# Revit family: 310-WC-4.8
name_source: partatom
category: Plumbing Fixtures
revit_build: Autodesk Revit 2014 (Build: 20130308_1515(x64)
units: mm (PartAtom-declared; Revit-internal decimal feet)

## types (1)
- 310-WC-4.8
    CW Connection = Yes
    Certification = http://www.helvex.com.mx
    Chrome = Brass Chromed
    Compliance = NOM-005-CONAGUA-1996
    Connection = 1" Feeding Connection
    Description = 1.268 gpf 32 Or 38 Exposed WC Flush Valve With Treadle
    Documentation = http://www.helvex.com.mx
    Features = To Be Used With 3/4" (19 mm) Spud
    Manufacturer = Helvex
    Max. Working Pressure = 85.3 psi
    Maximum Consumption = 1.26 gpf
    Min. Working Pressure = 14.2 psi
    Model = 310-WC-4.8
    Note = Feeding Pipe Must be (1 1/4") and Connect a (1 1/4" - 1") Reductor to Stop Valve
    Type Comments = Fluxómetros
    URL = http://www.helvex.com.mx
    Vent Connection = Yes
    Waste Connection = Yes

## geometry (parser evidence)
native form markers: Sweep x1
no freeform markers — native parametric forms only
